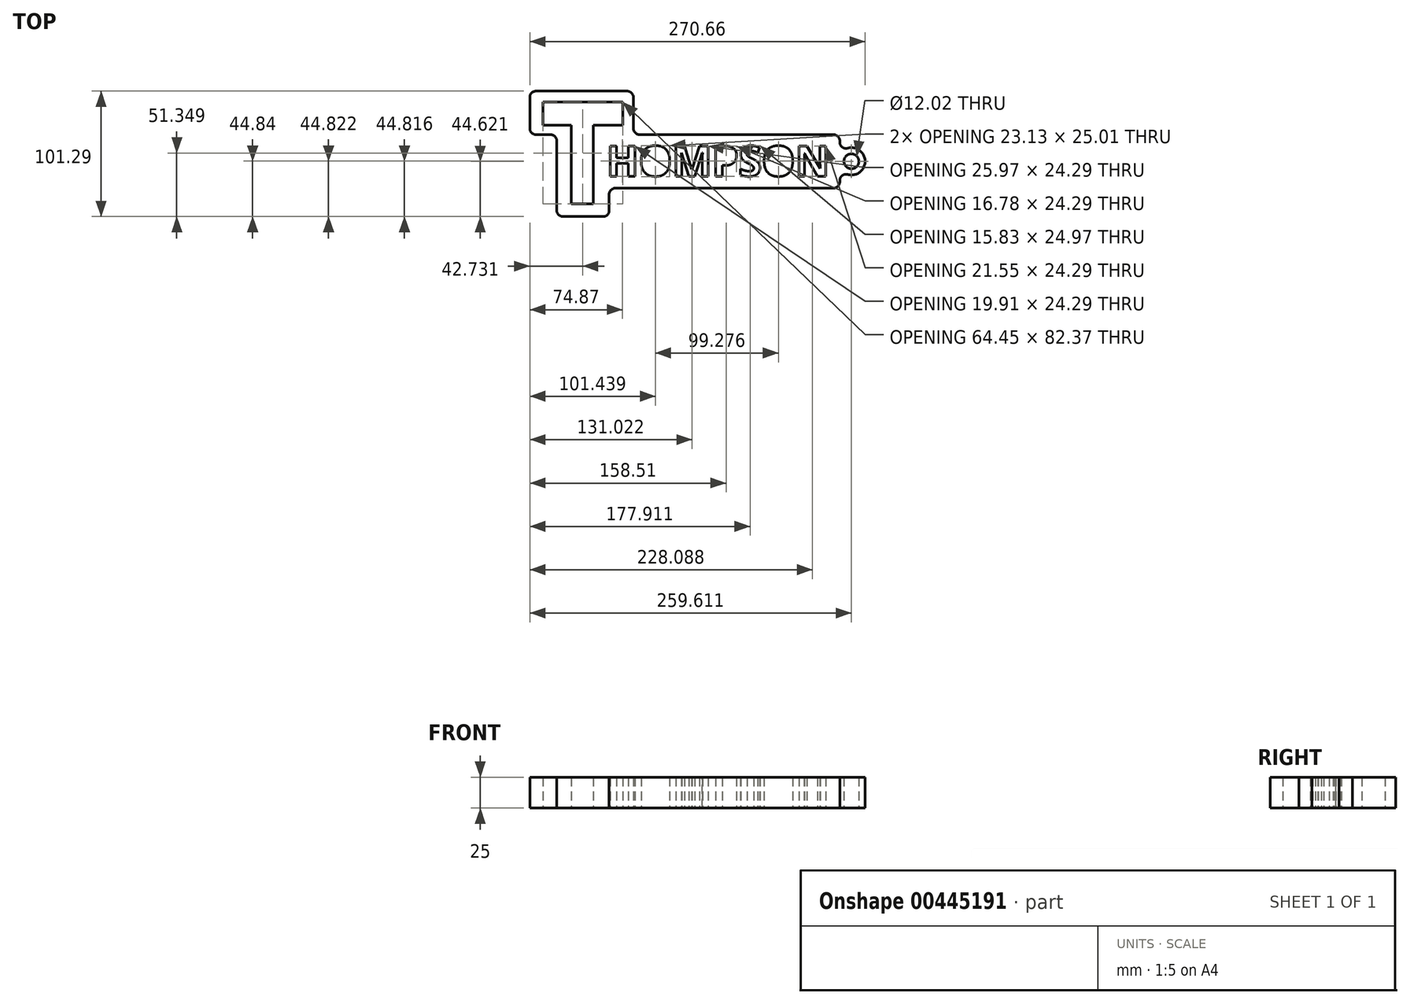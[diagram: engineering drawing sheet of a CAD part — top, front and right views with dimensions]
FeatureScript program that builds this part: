
annotation { "Feature Type Name" : "Feature", "Feature Type Description" : "" }
export const myFeature = defineFeature(function(context is Context, id is Id, definition is map)
    precondition{}
    {
        {
            var Q0;
            Q0=qCreatedBy(makeId("Top.planeOp"),FACE);
            var sketch = newSketch(context, id + "F0", { "sketchPlane" : qUnion([Q0])});
            skLineSegment(sketch, "E0", {"start": v(-44.32, -57.17) * mm, "end": v(22.22, -57.17) * mm});
            skLineSegment(sketch, "E1", {"start": v(22.22, -57.17) * mm, "end": v(22.22, -34.15) * mm});
            skLineSegment(sketch, "E2", {"start": v(22.22, -34.15) * mm, "end": v(208.39, -34.15) * mm});
            skLineSegment(sketch, "E3", {"start": v(208.39, -34.15) * mm, "end": v(208.39, 9.05) * mm});
            skLineSegment(sketch, "E4", {"start": v(208.39, 9.05) * mm, "end": v(41.83, 9.05) * mm});
            skLineSegment(sketch, "E5", {"start": v(41.83, 9.05) * mm, "end": v(41.83, 44.12) * mm});
            skLineSegment(sketch, "E6", {"start": v(41.83, 44.12) * mm, "end": v(-41.86, 44.12) * mm});
            skPoint(sketch, "E7.centerSnap0", {"position": v(230.68, -13.62) * mm});
            skLineSegment(sketch, "E8", {"start": v(33.1, 35.36) * mm, "end": v(33.1, 16.68) * mm});
            skLineSegment(sketch, "E9", {"start": v(33.1, 16.68) * mm, "end": v(9.45, 16.68) * mm});
            skLineSegment(sketch, "E10", {"start": v(9.45, 16.68) * mm, "end": v(9.45, -47) * mm});
            skLineSegment(sketch, "E11", {"start": v(9.45, -47) * mm, "end": v(-8.47, -47) * mm});
            skLineSegment(sketch, "E12", {"start": v(-8.47, -47) * mm, "end": v(-8.47, 16.68) * mm});
            skLineSegment(sketch, "E13", {"start": v(-8.47, 16.68) * mm, "end": v(-31.35, 16.68) * mm});
            skLineSegment(sketch, "E14", {"start": v(-31.35, 16.68) * mm, "end": v(-31.35, 35.36) * mm});
            skLineSegment(sketch, "E15", {"start": v(-31.35, 35.36) * mm, "end": v(33.1, 35.36) * mm});
            skText(sketch, "E16", { "text": "HOMPSON", "fontName": "OpenSans-Bold.ttf"});
            skLineSegment(sketch, "E17", {"start": v(-41.86, 44.12) * mm, "end": v(-41.86, -57.17) * mm});
            skLineSegment(sketch, "E18", {"start": v(-20.11, -57.17) * mm, "end": v(-20.11, 0) * mm});
            skLineSegment(sketch, "E19", {"start": v(-44.32, -57.17) * mm, "end": v(-41.86, -57.17) * mm});
            skCircle(sketch, "E20", {"center": v(217.75, -12.55) * mm, "radius": 11.05 * mm});
            skPoint(sketch, "E20.centerSnap0", {"position": v(208.39, -12.55) * mm});
            skCircle(sketch, "E21", {"center": v(217.75, -12.55) * mm, "radius": 6 * mm});
            skLineSegment(sketch, "E22", {"start": v(-20.11, 0) * mm, "end": v(-20.11, 9.05) * mm});
            skLineSegment(sketch, "E23", {"start": v(-20.11, 9.05) * mm, "end": v(-41.86, 9.05) * mm});
            const initialGuessF0  = {"E16": [0.02, -0.0245, 1, 0, 0.0245]};
            skSetInitialGuess(sketch, initialGuessF0);
            skSolve(sketch);
        }
        {
            var Q0;
            {var subQ3=sQuery(id+"F0.wireOp",EDGE,"E1");Q0=makeQuery(id+"F0.imprint","IMPRINT",FACE,{"disambiguationData":[TD([[makeQuery(id+"F0.imprint","IMPRINT",EDGE,{"derivedFrom":subQ3}),1.0]])]});}
            var Q1;
            {var subQ0=sQuery(id+"F0.wireOp",EDGE,"ME1WsGLH-2yKd-NUTf-9sHM-CfuZ7klpYuch");Q1=makeQuery(id+"F0.imprint","IMPRINT",FACE,{"disambiguationData":[TD([[makeQuery(id+"F0.imprint","IMPRINT",EDGE,{"derivedFrom":subQ0}),1.0]])]});}
            var Q2;
            Q2=makeQuery(id+"F0.imprint","IMPRINT",FACE,{"disambiguationData":[TD([[makeQuery(id+"F0.imprint","IMPRINT",EDGE,{"derivedFrom":sQuery(id+"F0.wireOp",EDGE,"klbQo2Lz-e63M-SSzw-cDLi-G3vKxpFZVOjJ")}),-1.0]])]});
            var Q3;
            Q3=makeQuery(id+"F0.imprint","IMPRINT",FACE,{"disambiguationData":[TD([[makeQuery(id+"F0.imprint","IMPRINT",EDGE,{"derivedFrom":sQuery(id+"F0.wireOp",EDGE,"E21")}),-1.0]])]});
            var Q4;
            {var subQ0=sQuery(id+"F0.wireOp",EDGE,"E20");var subQ1=sQuery(id+"F0.wireOp",EDGE,"E3");var subQ2=makeQuery(id+"F0.imprint","INTERSECT",VERTEX,{"disambiguationData":[OD(0.0)],"derivedFrom":[subQ1,subQ0]});Q4=makeQuery(id+"F0.imprint","IMPRINT",FACE,{"disambiguationData":[TD([[makeQuery(id+"F0.imprint","IMPRINT",EDGE,{"disambiguationData":[TD([[subQ2,-1.0]])],"derivedFrom":subQ1}),1.0]])]});}
            extrude(context, id + "F1", {"entities" : qUnion([Q0, Q1, Q2, Q3, Q4]), "depth" : 25 * mm});
        }
        {
            var Q0;
            {var subQ0=sQuery(id+"F0.wireOp",EDGE,"E20");var subQ1=sQuery(id+"F0.wireOp",EDGE,"E3");Q0=makeQuery(id+"F1.opExtrude","SWEPT_EDGE",EDGE,{"disambiguationData":[OSD([subQ1,subQ0]),TDD([makeQuery(id+"F0.imprint","INTERSECT",VERTEX,{"disambiguationData":[OD(1.0)],"derivedFrom":[subQ1,subQ0]})])]});}
            var Q1;
            {var subQ0=sQuery(id+"F0.wireOp",EDGE,"E20");var subQ1=sQuery(id+"F0.wireOp",EDGE,"E3");Q1=makeQuery(id+"F1.opExtrude","SWEPT_EDGE",EDGE,{"disambiguationData":[OSD([subQ1,subQ0]),TDD([makeQuery(id+"F0.imprint","INTERSECT",VERTEX,{"disambiguationData":[OD(0.0)],"derivedFrom":[subQ1,subQ0]})])]});}
            var Q2;
            Q2=makeQuery(id+"F1.opExtrude","SWEPT_EDGE",EDGE,{"disambiguationData":[OSD([sQuery(id+"F0.wireOp",EDGE,"E1"),sQuery(id+"F0.wireOp",EDGE,"E2")])]});
            var Q3;
            Q3=makeQuery(id+"F1.opExtrude","SWEPT_EDGE",EDGE,{"disambiguationData":[OSD([sQuery(id+"F0.wireOp",EDGE,"E0"),sQuery(id+"F0.wireOp",EDGE,"E1")])]});
            var Q4;
            Q4=makeQuery(id+"F1.opExtrude","SWEPT_EDGE",EDGE,{"disambiguationData":[OSD([sQuery(id+"F0.wireOp",EDGE,"E0"),sQuery(id+"F0.wireOp",EDGE,"E18")])]});
            var Q5;
            Q5=makeQuery(id+"F1.opExtrude","SWEPT_EDGE",EDGE,{"disambiguationData":[OSD([sQuery(id+"F0.wireOp",EDGE,"E2"),sQuery(id+"F0.wireOp",EDGE,"E3")])]});
            var Q6;
            Q6=makeQuery(id+"F1.opExtrude","SWEPT_EDGE",EDGE,{"disambiguationData":[OSD([sQuery(id+"F0.wireOp",EDGE,"E22"),sQuery(id+"F0.wireOp",EDGE,"E23")])]});
            var Q7;
            Q7=makeQuery(id+"F1.opExtrude","SWEPT_EDGE",EDGE,{"disambiguationData":[OSD([sQuery(id+"F0.wireOp",EDGE,"E17"),sQuery(id+"F0.wireOp",EDGE,"E23")])]});
            var Q8;
            Q8=makeQuery(id+"F1.opExtrude","SWEPT_EDGE",EDGE,{"disambiguationData":[OSD([sQuery(id+"F0.wireOp",EDGE,"E6"),sQuery(id+"F0.wireOp",EDGE,"E17")])]});
            var Q9;
            Q9=makeQuery(id+"F1.opExtrude","SWEPT_EDGE",EDGE,{"disambiguationData":[OSD([sQuery(id+"F0.wireOp",EDGE,"E5"),sQuery(id+"F0.wireOp",EDGE,"E6")])]});
            var Q10;
            Q10=makeQuery(id+"F1.opExtrude","SWEPT_EDGE",EDGE,{"disambiguationData":[OSD([sQuery(id+"F0.wireOp",EDGE,"E4"),sQuery(id+"F0.wireOp",EDGE,"E5")])]});
            var Q11;
            Q11=makeQuery(id+"F1.opExtrude","SWEPT_EDGE",EDGE,{"disambiguationData":[OSD([sQuery(id+"F0.wireOp",EDGE,"E3"),sQuery(id+"F0.wireOp",EDGE,"E4")])]});
            fillet(context, id + "F2", {"entities" : qUnion([Q0, Q1, Q2, Q3, Q4, Q5, Q6, Q7, Q8, Q9, Q10, Q11]), "radius" : 5 * mm, "tangentPropagation" : true, "allowEdgeOverflow" : false});
        }
    });
